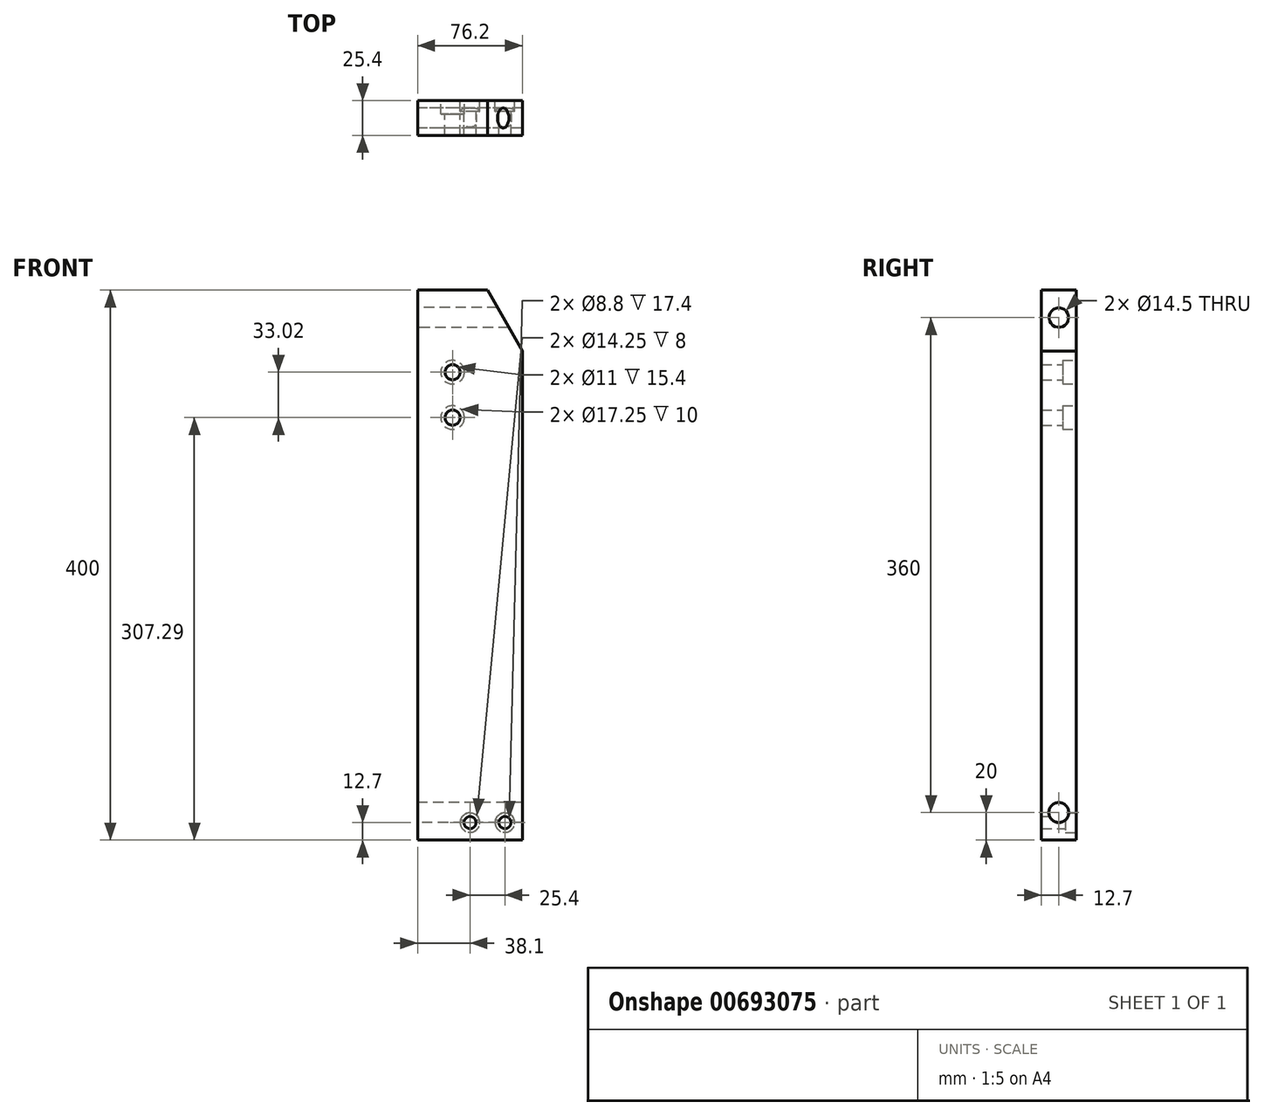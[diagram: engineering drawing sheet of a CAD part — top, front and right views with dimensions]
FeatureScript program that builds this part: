
annotation { "Feature Type Name" : "Feature", "Feature Type Description" : "" }
export const myFeature = defineFeature(function(context is Context, id is Id, definition is map)
    precondition{}
    {
        {
            var Q0;
            Q0=qCreatedBy(makeId("Front.planeOp"),FACE);
            var sketch = newSketch(context, id + "F0", { "sketchPlane" : qUnion([Q0])});
            skLineSegment(sketch, "E0", {"start": v(0, 0) * mm, "end": v(0, 400) * mm});
            skLineSegment(sketch, "E1", {"start": v(0, 400) * mm, "end": v(50.8, 400) * mm});
            skLineSegment(sketch, "E2", {"start": v(0, 0) * mm, "end": v(76.2, 0) * mm});
            skLineSegment(sketch, "E3", {"start": v(76.2, 0) * mm, "end": v(76.2, 355.6) * mm});
            skLineSegment(sketch, "E4", {"start": v(76.2, 355.6) * mm, "end": v(50.8, 400) * mm});
            skSolve(sketch);
        }
        {
            var Q0;
            Q0=makeQuery(id+"F0.imprint","IMPRINT",FACE,{"disambiguationData":[TD([[makeQuery(id+"F0.imprint","IMPRINT",EDGE,{"derivedFrom":sQuery(id+"F0.wireOp",EDGE,"E0")}),-1.0]])]});
            extrude(context, id + "F1", {"entities" : qUnion([Q0]), "depth" : 25.4 * mm, "offsetDistance" : 25.4 * mm});
        }
        {
            var Q0;
            Q0=makeQuery(id+"F1.opExtrude","SWEPT_FACE",FACE,{"disambiguationData":[OSD([sQuery(id+"F0.wireOp",EDGE,"E0")])]});
            var sketch = newSketch(context, id + "F2", { "sketchPlane" : qUnion([Q0])});
            skLineSegment(sketch, "E5", {"start": v(12.7, 0) * mm, "end": v(12.7, 20) * mm});
            skLineSegment(sketch, "E6", {"start": v(12.7, 400) * mm, "end": v(12.7, 380) * mm});
            skSolve(sketch);
        }
        {
            var Q0;
            Q0=sQuery(id+"F2.wireOp",VERTEX,"E5.end");
            var Q1;
            Q1=sQuery(id+"F2.wireOp",VERTEX,"E6.end");
            var Q2;
            Q2=makeQuery(id+"F1.opExtrude","SWEPT_BODY",BODY,{"disambiguationData":[OSD([sQuery(id+"F0.wireOp",EDGE,"E0"),sQuery(id+"F0.wireOp",EDGE,"E1"),sQuery(id+"F0.wireOp",EDGE,"E2"),sQuery(id+"F0.wireOp",EDGE,"E3"),sQuery(id+"F0.wireOp",EDGE,"E4")])]});
            hole(context, id + "F3", {"style" : HoleStyle.SIMPLE, "endStyle" : HoleEndStyle.THROUGH, "standardTappedOrClearance" : lookupTablePath({ "standard" : "ISO", "engagement" : "75%", "pitch" : "1.5 mm", "size" : "M16", "type" : "Tapped" }), "standardBlindInLast" : lookupTablePath({ "standard" : "ISO", "engagement" : "75%", "pitch" : "1.5 mm", "size" : "M16", "type" : "Tapped" }), "holeDiameter" : 14.5 * mm, "majorDiameter" : 16 * mm, "showTappedDepth" : true, "tappedDepth" : 19.4 * mm, "tapClearance" : 3, "locations" : qUnion([Q0, Q1]), "scope" : qUnion([Q2])});
        }
        {
            var Q0;
            Q0=makeQuery(id+"F1.opExtrude","CAP_FACE",FACE,{"disambiguationData":[OSD([sQuery(id+"F0.wireOp",EDGE,"E0"),sQuery(id+"F0.wireOp",EDGE,"E1"),sQuery(id+"F0.wireOp",EDGE,"E2"),sQuery(id+"F0.wireOp",EDGE,"E3"),sQuery(id+"F0.wireOp",EDGE,"E4")])],"isStart":true});
            var sketch = newSketch(context, id + "F4", { "sketchPlane" : qUnion([Q0])});
            skLineSegment(sketch, "E7", {"start": v(-76.2, 0) * mm, "end": v(-76.2, 12.7) * mm});
            skLineSegment(sketch, "E8", {"start": v(-76.2, 12.7) * mm, "end": v(-63.5, 12.7) * mm});
            skLineSegment(sketch, "E9", {"start": v(-63.5, 12.7) * mm, "end": v(-38.1, 12.7) * mm});
            skSolve(sketch);
        }
        {
            var Q0;
            Q0=sQuery(id+"F4.wireOp",VERTEX,"E9.start");
            var Q1;
            Q1=sQuery(id+"F4.wireOp",VERTEX,"E9.end");
            var Q2;
            Q2=makeQuery(id+"F1.opExtrude","SWEPT_BODY",BODY,{"disambiguationData":[OSD([sQuery(id+"F0.wireOp",EDGE,"E0"),sQuery(id+"F0.wireOp",EDGE,"E1"),sQuery(id+"F0.wireOp",EDGE,"E2"),sQuery(id+"F0.wireOp",EDGE,"E3"),sQuery(id+"F0.wireOp",EDGE,"E4")])]});
            hole(context, id + "F5", {"style" : HoleStyle.C_BORE, "endStyle" : HoleEndStyle.THROUGH, "standardTappedOrClearance" : lookupTablePath({ "standard" : "ISO", "fit" : "Normal", "size" : "M8", "type" : "Clearance" }), "standardBlindInLast" : lookupTablePath({ "fit" : "Standard", "standard" : "ISO", "size" : "M8", "type" : "Clearance" }), "holeDiameter" : 8.8 * mm, "cBoreDiameter" : 14.25 * mm, "cBoreDepth" : 8 * mm, "majorDiameter" : 8 * mm, "tappedDepth" : 19.4 * mm, "tapClearance" : 3, "locations" : qUnion([Q0, Q1]), "scope" : qUnion([Q2])});
        }
        {
            var Q0;
            Q0=makeQuery(id+"F1.opExtrude","CAP_FACE",FACE,{"disambiguationData":[OSD([sQuery(id+"F0.wireOp",EDGE,"E0"),sQuery(id+"F0.wireOp",EDGE,"E1"),sQuery(id+"F0.wireOp",EDGE,"E2"),sQuery(id+"F0.wireOp",EDGE,"E3"),sQuery(id+"F0.wireOp",EDGE,"E4")])],"isStart":true});
            var sketch = newSketch(context, id + "F6", { "sketchPlane" : qUnion([Q0])});
            skLineSegment(sketch, "E10", {"start": v(-25.4, 400) * mm, "end": v(-25.4, 340.3) * mm});
            skLineSegment(sketch, "E11", {"start": v(-25.4, 340.3) * mm, "end": v(-25.4, 307.3) * mm});
            skSolve(sketch);
        }
        {
            var Q0;
            Q0=sQuery(id+"F6.wireOp",VERTEX,"E11.start");
            var Q1;
            Q1=sQuery(id+"F6.wireOp",VERTEX,"E11.end");
            var Q2;
            Q2=makeQuery(id+"F1.opExtrude","SWEPT_BODY",BODY,{"disambiguationData":[OSD([sQuery(id+"F0.wireOp",EDGE,"E0"),sQuery(id+"F0.wireOp",EDGE,"E1"),sQuery(id+"F0.wireOp",EDGE,"E2"),sQuery(id+"F0.wireOp",EDGE,"E3"),sQuery(id+"F0.wireOp",EDGE,"E4")])]});
            hole(context, id + "F7", {"style" : HoleStyle.C_BORE, "endStyle" : HoleEndStyle.THROUGH, "standardTappedOrClearance" : lookupTablePath({ "standard" : "ISO", "fit" : "Normal", "size" : "M10", "type" : "Clearance" }), "standardBlindInLast" : lookupTablePath({ "fit" : "Standard", "standard" : "ISO", "size" : "M10", "type" : "Clearance" }), "holeDiameter" : 11 * mm, "cBoreDiameter" : 17.25 * mm, "cBoreDepth" : 10 * mm, "majorDiameter" : 8 * mm, "tappedDepth" : 19.4 * mm, "tapClearance" : 3, "locations" : qUnion([Q0, Q1]), "scope" : qUnion([Q2])});
        }
    });
